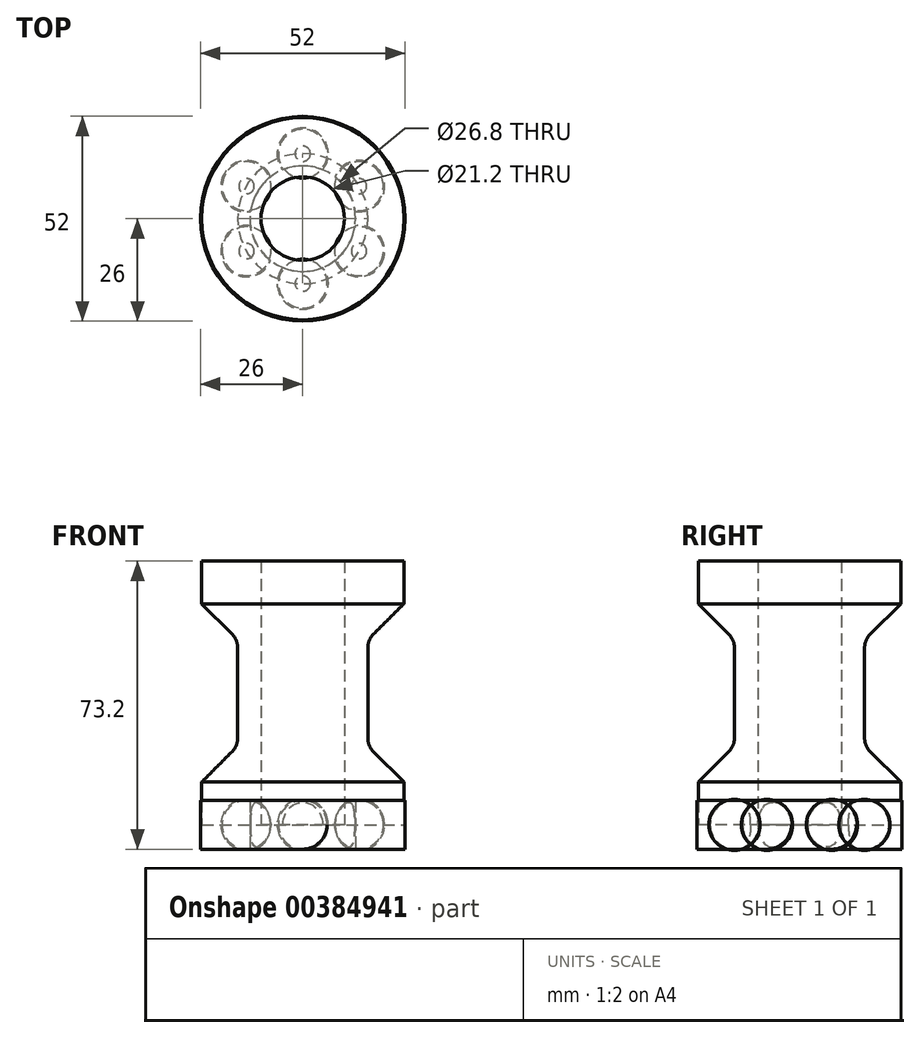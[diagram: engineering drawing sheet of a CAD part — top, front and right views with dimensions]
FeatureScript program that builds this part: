
annotation { "Feature Type Name" : "Feature", "Feature Type Description" : "" }
export const myFeature = defineFeature(function(context is Context, id is Id, definition is map)
    precondition{}
    {
        {
            assignVariable(context, id + "F0", {"name" : "InnerRadius", "anyValue" : 10});
        }
        {
            assignVariable(context, id + "F1", {"name" : "OutterRadius", "anyValue" : 26});
        }
        {
            assignVariable(context, id + "F2", {"name" : "Thickness", "anyValue" : 3});
        }
        {
            assignVariable(context, id + "F3", {"name" : "Segments", "anyValue" : 6});
        }
        {
            assignVariable(context, id + "F4", {"name" : "Tolerance", "anyValue" : .3});
        }
        {
            assignVariable(context, id + "F5", {"name" : "BallRadius", "anyValue" : (getVariable(context, 'OutterRadius') - getVariable(context, 'InnerRadius') - 2 * getVariable(context, 'Tolerance') - getVariable(context, 'Thickness')) / 2});
        }
        {
            var Q0;
            Q0=qCreatedBy(makeId("Top.planeOp"),FACE);
            var sketch = newSketch(context, id + "F6", { "sketchPlane" : qUnion([Q0])});
            skCircle(sketch, "E0", {"center": v(0, 0) * mm, "radius": 10 * mm, "construction": true});
            skCircle(sketch, "E1", {"center": v(0, 0) * mm, "radius": 26 * mm, "construction": true});
            skLineSegment(sketch, "E2", {"start": v(0, 0) * mm, "end": v(0, 26) * mm, "construction": true});
            skCircle(sketch, "E3.0", {"center": v(0, 0) * mm, "radius": 23 * mm, "construction": true});
            skCircle(sketch, "E4", {"center": v(0, 0) * mm, "radius": 16.5 * mm, "construction": true});
            skCircle(sketch, "E5", {"center": v(0, 16.5) * mm, "radius": 6.2 * mm, "construction": true});
            skCircle(sketch, "E6.0", {"center": v(0, 16.5) * mm, "radius": 6.5 * mm, "construction": true});
            skCircle(sketch, "E7", {"center": v(0, 0) * mm, "radius": 13.4 * mm, "construction": true});
            skCircle(sketch, "E8", {"center": v(0, 0) * mm, "radius": 13.25 * mm, "construction": true});
            skSolve(sketch);
        }
        {
            var Q0;
            Q0=qCreatedBy(makeId("Top.planeOp"),FACE);
            var sketch = newSketch(context, id + "F7", { "sketchPlane" : qUnion([Q0])});
            skCircle(sketch, "E9.0", {"center": v(0, 0) * mm, "radius": 13.4 * mm});
            skCircle(sketch, "E9.1", {"center": v(0, 0) * mm, "radius": 26 * mm});
            skSolve(sketch);
        }
        {
            var Q0;
            Q0 = qSketchRegion(id + "F7", true);
            extrude(context, id + "F8", {"entities" : qUnion([Q0]), "endBound" : BoundingType.SYMMETRIC, "depth" : (2 * getVariable(context, 'BallRadius')) * mm});
        }
        {
            var Q0;
            Q0=qCreatedBy(makeId("Front.planeOp"),FACE);
            var sketch = newSketch(context, id + "F9", { "sketchPlane" : qUnion([Q0])});
            skLineSegment(sketch, "E10", {"start": v(0, 0) * mm, "end": v(0, 33.35) * mm, "construction": true});
            skSolve(sketch);
        }
        {
            var Q0;
            Q0=qCreatedBy(makeId("Top.planeOp"),FACE);
            var sketch = newSketch(context, id + "F10", { "sketchPlane" : qUnion([Q0])});
            skCircle(sketch, "E11.0", {"center": v(0, 16.5) * mm, "radius": 6.5 * mm});
            skPoint(sketch, "E12.center", {"position": v(0, 0) * mm});
            skLineSegment(sketch, "E13.0", {"start": v(0, 0) * mm, "end": v(0, 26) * mm});
            skSolve(sketch);
        }
        {
            var Q0;
            {var subQ0=sQuery(id+"F10.wireOp",EDGE,"E13.0");var subQ1=sQuery(id+"F10.wireOp",EDGE,"E11.0");var subQ2=makeQuery(id+"F10.imprint","INTERSECT",VERTEX,{"disambiguationData":[OD(0.0)],"derivedFrom":[subQ1,subQ0]});Q0=makeQuery(id+"F10.imprint","IMPRINT",FACE,{"disambiguationData":[TD([[makeQuery(id+"F10.imprint","IMPRINT",EDGE,{"disambiguationData":[TD([[subQ2,1.0]])],"derivedFrom":subQ1}),1.0]])]});}
            var Q1;
            Q1=sQuery(id+"F6.wireOp",EDGE,"E2");
            revolve(context, id + "F11", {"entities" : qUnion([Q0]), "axis" : qUnion([Q1]), "revolveType" : RevolveType.FULL});
        }
        {
            var Q0;
            Q0=makeQuery(id+"F11.opRevolve","SWEPT_BODY",BODY,{"disambiguationData":[OSD([sQuery(id+"F10.wireOp",EDGE,"E11.0"),sQuery(id+"F10.wireOp",EDGE,"E13.0")])]});
            var Q1;
            Q1=sQuery(id+"F9.wireOp",EDGE,"E10");
            circularPattern(context, id + "F12", {"operationType" : NewBodyOperationType.REMOVE, "entities" : qUnion([Q0]), "axis" : qUnion([Q1]), "angle" : 360 * degree, "instanceCount" : getVariable(context, 'Segments'), "equalSpace" : true});
        }
        {
            var Q0;
            Q0=qCreatedBy(makeId("Top.planeOp"),FACE);
            var sketch = newSketch(context, id + "F13", { "sketchPlane" : qUnion([Q0])});
            skCircle(sketch, "E14.0", {"center": v(0, 16.5) * mm, "radius": 6.2 * mm});
            skLineSegment(sketch, "E15.0", {"start": v(0, 0) * mm, "end": v(0, 26) * mm});
            skSolve(sketch);
        }
        {
            var Q0;
            {var subQ0=sQuery(id+"F13.wireOp",EDGE,"E15.0");var subQ1=sQuery(id+"F13.wireOp",EDGE,"E14.0");var subQ2=makeQuery(id+"F13.imprint","INTERSECT",VERTEX,{"disambiguationData":[OD(0.0)],"derivedFrom":[subQ1,subQ0]});Q0=makeQuery(id+"F13.imprint","IMPRINT",FACE,{"disambiguationData":[TD([[makeQuery(id+"F13.imprint","IMPRINT",EDGE,{"disambiguationData":[TD([[subQ2,1.0]])],"derivedFrom":subQ1}),1.0]])]});}
            var Q1;
            Q1=sQuery(id+"F13.wireOp",EDGE,"E15.0");
            revolve(context, id + "F14", {"entities" : qUnion([Q0]), "axis" : qUnion([Q1]), "revolveType" : RevolveType.FULL});
        }
        {
            var Q0;
            Q0=makeQuery(id+"F14.opRevolve","SWEPT_BODY",BODY,{"disambiguationData":[OSD([sQuery(id+"F13.wireOp",EDGE,"E14.0"),sQuery(id+"F13.wireOp",EDGE,"E15.0")])]});
            var Q1;
            Q1=sQuery(id+"F9.wireOp",EDGE,"E10");
            circularPattern(context, id + "F15", {"entities" : qUnion([Q0]), "axis" : qUnion([Q1]), "angle" : 360 * degree, "instanceCount" : getVariable(context, 'Segments'), "equalSpace" : true});
        }
        {
            var Q0;
            Q0=qCreatedBy(makeId("Top.planeOp"),FACE);
            var sketch = newSketch(context, id + "F16", { "sketchPlane" : qUnion([Q0])});
            skCircle(sketch, "E16.0", {"center": v(0, 0) * mm, "radius": 10 * mm});
            skCircle(sketch, "E16.1", {"center": v(0, 0) * mm, "radius": 26 * mm});
            skCircle(sketch, "E17.0", {"center": v(0, 0) * mm, "radius": 10.3 * mm});
            skCircle(sketch, "E18.0", {"center": v(0, 0) * mm, "radius": 25.7 * mm});
            skCircle(sketch, "E19.0", {"center": v(0, 0) * mm, "radius": 10.6 * mm});
            skSolve(sketch);
        }
        {
            var Q0;
            Q0=makeQuery(id+"F16.imprint","IMPRINT",FACE,{"disambiguationData":[TD([[makeQuery(id+"F16.imprint","IMPRINT",EDGE,{"derivedFrom":sQuery(id+"F16.wireOp",EDGE,"E18.0")}),1.0]])]});
            extrude(context, id + "F17", {"entities" : qUnion([Q0]), "depth" : 67 * mm, "offsetDistance" : 25 * mm});
        }
        {
            var Q0;
            Q0=qCreatedBy(makeId("Front.planeOp"),FACE);
            var sketch = newSketch(context, id + "F18", { "sketchPlane" : qUnion([Q0])});
            skLineSegment(sketch, "E20", {"start": v(0, 0) * mm, "end": v(0, 79.17) * mm});
            skLineSegment(sketch, "E21", {"start": v(0, 0) * mm, "end": v(26.53, 0) * mm});
            skLineSegment(sketch, "E22", {"start": v(26.53, 0) * mm, "end": v(26.53, 10) * mm});
            skLineSegment(sketch, "E23", {"start": v(26.53, 10) * mm, "end": v(6.53, 10) * mm});
            skLineSegment(sketch, "E24", {"start": v(11.53, 27.07) * mm, "end": v(11.53, 39.93) * mm});
            skLineSegment(sketch, "E25", {"start": v(11.53, 57) * mm, "end": v(26.53, 57) * mm});
            skLineSegment(sketch, "E26", {"start": v(26.53, 57) * mm, "end": v(26.53, 69) * mm});
            skLineSegment(sketch, "E27", {"start": v(26.53, 69) * mm, "end": v(34.73, 69) * mm});
            skLineSegment(sketch, "E28", {"start": v(34.73, 69) * mm, "end": v(34.73, 0) * mm});
            skLineSegment(sketch, "E29", {"start": v(34.73, 0) * mm, "end": v(26.53, 0) * mm});
            skLineSegment(sketch, "E30", {"start": v(26.53, 10) * mm, "end": v(18, 18.54) * mm});
            skLineSegment(sketch, "E31", {"start": v(26.53, 57) * mm, "end": v(18, 48.46) * mm});
            skPoint(sketch, "E32.newPointB", {"position": v(11.53, 57) * mm});
            skPoint(sketch, "E33.newPointB", {"position": v(11.53, 10) * mm});
            skLineSegment(sketch, "E34.0", {"start": v(16.53, 22.07) * mm, "end": v(16.53, 44.93) * mm});
            skArc(sketch, "E35.filletArc", {"start": v(18, 48.46) * mm, "mid": v(16.91, 46.84) * mm, "end": v(16.53, 44.93) * mm});
            skArc(sketch, "E36.filletArc", {"start": v(16.53, 22.07) * mm, "mid": v(16.91, 20.16) * mm, "end": v(18, 18.54) * mm});
            skSolve(sketch);
        }
        {
            var Q0;
            Q0=makeQuery(id+"F18.imprint","IMPRINT",FACE,{"disambiguationData":[TD([[makeQuery(id+"F18.imprint","IMPRINT",EDGE,{"derivedFrom":sQuery(id+"F18.wireOp",EDGE,"E22")}),-1.0]])]});
            var Q1;
            Q1=sQuery(id+"F18.wireOp",EDGE,"E20");
            revolve(context, id + "F19", {"operationType" : NewBodyOperationType.REMOVE, "entities" : qUnion([Q0]), "axis" : qUnion([Q1]), "revolveType" : RevolveType.FULL, "oppositeDirection" : true});
        }
    });
